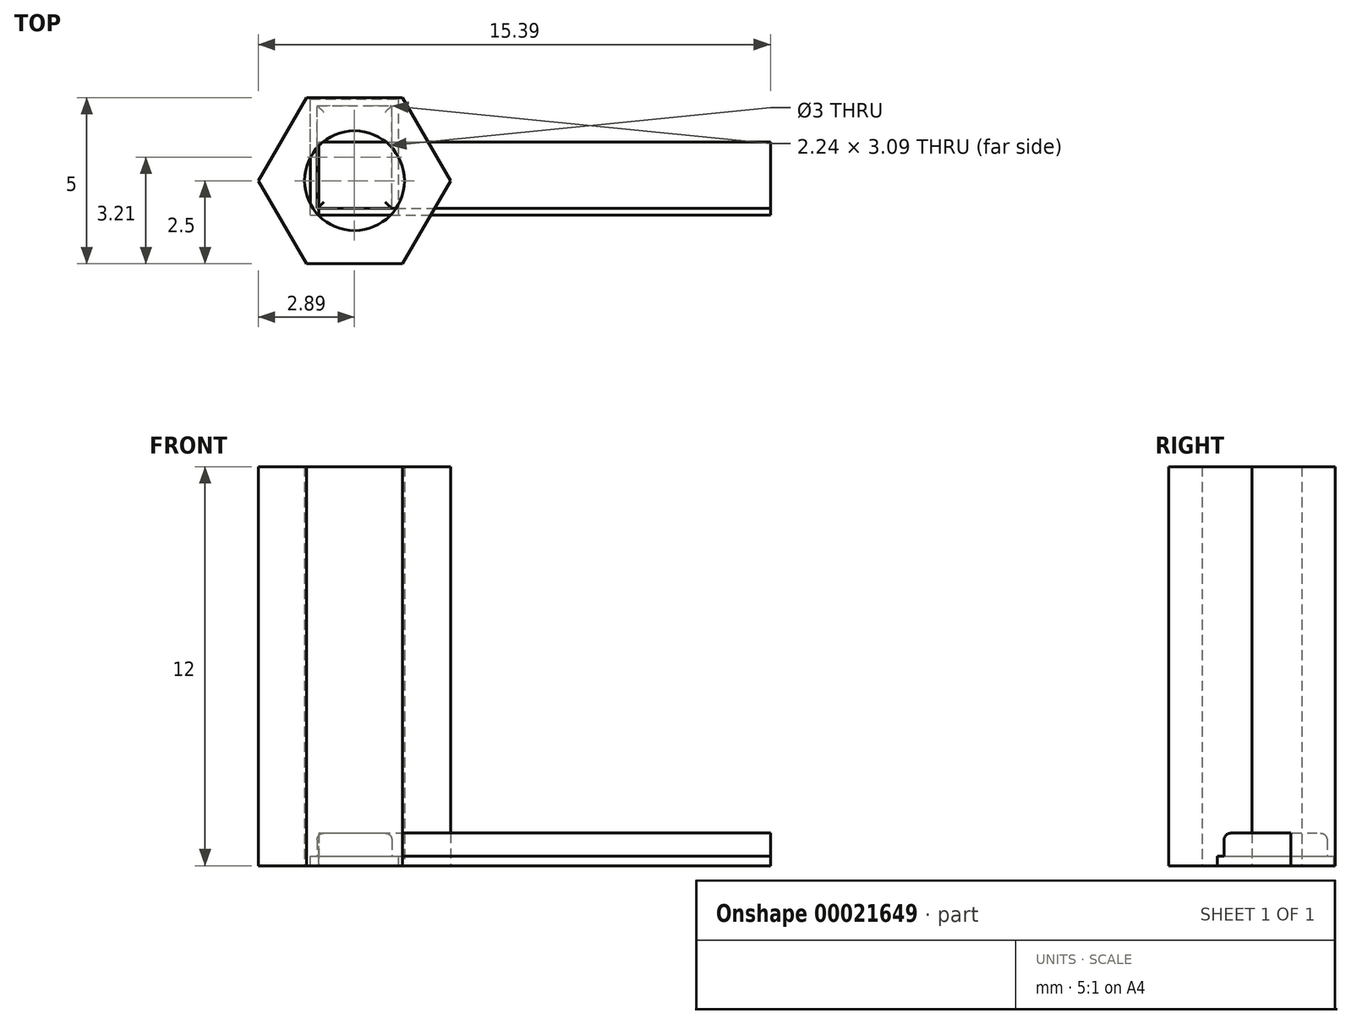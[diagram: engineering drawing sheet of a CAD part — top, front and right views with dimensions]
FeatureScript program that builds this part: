
annotation { "Feature Type Name" : "Feature", "Feature Type Description" : "" }
export const myFeature = defineFeature(function(context is Context, id is Id, definition is map)
    precondition{}
    {
        {
            var Q0;
            Q0=qCreatedBy(makeId("Front.planeOp"),FACE);
            var sketch = newSketch(context, id + "F0", { "sketchPlane" : qUnion([Q0])});
            skLineSegment(sketch, "E0.bottom", {"start": v(-1.12, 0.3) * mm, "end": v(1.12, 0.3) * mm});
            skPoint(sketch, "E1", {"position": v(0, 0.3) * mm});
            skPoint(sketch, "E2.visualSharp", {"position": v(1.12, 0.98) * mm});
            skLineSegment(sketch, "E3.top", {"start": v(-1.32, 0.3) * mm, "end": v(1.32, 0.3) * mm});
            skLineSegment(sketch, "E0.top", {"start": v(-0.92, 0.98) * mm, "end": v(0.92, 0.98) * mm});
            skPoint(sketch, "E4.visualSharp", {"position": v(-1.12, 0.98) * mm});
            skLineSegment(sketch, "E3.bottom", {"start": v(-1.32, 0) * mm, "end": v(1.32, 0) * mm});
            skPoint(sketch, "E5", {"position": v(0, 0) * mm});
            skLineSegment(sketch, "E0.right", {"start": v(1.12, 0.3) * mm, "end": v(1.12, 0.78) * mm});
            skLineSegment(sketch, "E3.left", {"start": v(-1.32, 0) * mm, "end": v(-1.32, 0.3) * mm});
            skLineSegment(sketch, "E0.left", {"start": v(-1.12, 0.3) * mm, "end": v(-1.12, 0.78) * mm});
            skLineSegment(sketch, "E3.right", {"start": v(1.32, 0) * mm, "end": v(1.32, 0.3) * mm});
            skArc(sketch, "E2.filletArc", {"start": v(1.12, 0.78) * mm, "mid": v(1.06, 0.92) * mm, "end": v(0.92, 0.98) * mm});
            skArc(sketch, "E4.filletArc", {"start": v(-0.92, 0.98) * mm, "mid": v(-1.06, 0.92) * mm, "end": v(-1.12, 0.78) * mm});
            skLineSegment(sketch, "E6.bottom", {"start": v(-0.13, 0) * mm, "end": v(0.13, 0) * mm, "construction": true});
            skLineSegment(sketch, "E6.top", {"start": v(-0.12, 0.3) * mm, "end": v(0.12, 0.3) * mm, "construction": true});
            skLineSegment(sketch, "E6.left", {"start": v(-0.13, 0) * mm, "end": v(-0.12, 0.3) * mm, "construction": true});
            skLineSegment(sketch, "E6.right", {"start": v(0.12, 0) * mm, "end": v(0.13, 0.3) * mm, "construction": true});
            skSolve(sketch);
        }
        {
            var Q0;
            Q0=qCreatedBy(makeId("Right.planeOp"),FACE);
            var sketch = newSketch(context, id + "F1", { "sketchPlane" : qUnion([Q0])});
            skLineSegment(sketch, "E7.bottom", {"start": v(-0.84, 0.3) * mm, "end": v(2.26, 0.3) * mm});
            skPoint(sketch, "E8", {"position": v(0, 0.3) * mm});
            skPoint(sketch, "E9.visualSharp", {"position": v(2.26, 0.98) * mm});
            skLineSegment(sketch, "E10.top", {"start": v(-1.04, 0.3) * mm, "end": v(2.46, 0.3) * mm});
            skLineSegment(sketch, "E7.top", {"start": v(-0.64, 0.98) * mm, "end": v(2.06, 0.98) * mm});
            skPoint(sketch, "E11.visualSharp", {"position": v(-0.84, 0.98) * mm});
            skLineSegment(sketch, "E10.bottom", {"start": v(-1.04, 0) * mm, "end": v(2.46, 0) * mm});
            skPoint(sketch, "E12", {"position": v(0, 0) * mm});
            skLineSegment(sketch, "E7.right", {"start": v(2.26, 0.3) * mm, "end": v(2.26, 0.78) * mm});
            skLineSegment(sketch, "E10.left", {"start": v(-1.04, 0) * mm, "end": v(-1.04, 0.3) * mm});
            skLineSegment(sketch, "E7.left", {"start": v(-0.84, 0.3) * mm, "end": v(-0.84, 0.78) * mm});
            skLineSegment(sketch, "E10.right", {"start": v(2.46, 0) * mm, "end": v(2.46, 0.3) * mm});
            skArc(sketch, "E9.filletArc", {"start": v(2.26, 0.78) * mm, "mid": v(2.2, 0.92) * mm, "end": v(2.06, 0.98) * mm});
            skArc(sketch, "E11.filletArc", {"start": v(-0.64, 0.98) * mm, "mid": v(-0.78, 0.92) * mm, "end": v(-0.84, 0.78) * mm});
            skLineSegment(sketch, "E13.bottom", {"start": v(-0.12, 0) * mm, "end": v(0.12, 0) * mm, "construction": true});
            skLineSegment(sketch, "E13.top", {"start": v(-0.12, 0.3) * mm, "end": v(0.13, 0.3) * mm, "construction": true});
            skLineSegment(sketch, "E13.left", {"start": v(-0.12, 0) * mm, "end": v(-0.12, 0.3) * mm, "construction": true});
            skLineSegment(sketch, "E13.right", {"start": v(0.13, 0) * mm, "end": v(0.13, 0.3) * mm, "construction": true});
            skPoint(sketch, "E14", {"position": v(0.71, 0.3) * mm});
            skPoint(sketch, "E15", {"position": v(0.7, 0.98) * mm});
            skSolve(sketch);
        }
        {
            var Q0;
            Q0=qCreatedBy(makeId("Right.planeOp"),FACE);
            var sketch = newSketch(context, id + "F2", { "sketchPlane" : qUnion([Q0])});
            skLineSegment(sketch, "E16", {"start": v(0.32, 7.81) * mm, "end": v(0, 8.13) * mm});
            skLineSegment(sketch, "E17", {"start": v(1.17, 2.29) * mm, "end": v(1.17, 0) * mm});
            skLineSegment(sketch, "E18.MirrorCS", {"start": v(-1.17, 2.29) * mm, "end": v(-1.17, 0) * mm});
            skLineSegment(sketch, "E19", {"start": v(0, 8.13) * mm, "end": v(-0.32, 7.81) * mm});
            skLineSegment(sketch, "E20", {"start": v(-0.32, 7.81) * mm, "end": v(0.32, 7.81) * mm});
            skLineSegment(sketch, "E21", {"start": v(0, -5.48) * mm, "end": v(0, 11.54) * mm, "construction": true});
            skLineSegment(sketch, "E22", {"start": v(-1.17, 0) * mm, "end": v(1.17, 0) * mm});
            skPoint(sketch, "E23", {"position": v(0, 0) * mm});
            skLineSegment(sketch, "E24", {"start": v(-1.17, 2.29) * mm, "end": v(1.17, 2.29) * mm});
            skLineSegment(sketch, "E25", {"start": v(-0.32, 7.81) * mm, "end": v(-0.32, -1.97) * mm});
            skLineSegment(sketch, "E26", {"start": v(-0.32, -1.97) * mm, "end": v(0, -2.29) * mm});
            skLineSegment(sketch, "E27", {"start": v(0.32, 7.81) * mm, "end": v(0.32, -1.97) * mm});
            skLineSegment(sketch, "E28", {"start": v(0.32, -1.97) * mm, "end": v(0, -2.29) * mm});
            skLineSegment(sketch, "E29", {"start": v(0.32, -1.97) * mm, "end": v(-0.32, -1.97) * mm});
            skSolve(sketch);
        }
        {
            var Q0;
            Q0=qCreatedBy(makeId("Top.planeOp"),FACE);
            var sketch = newSketch(context, id + "F3", { "sketchPlane" : qUnion([Q0])});
            skCircle(sketch, "E30.cCircle", {"center": v(0, 0) * mm, "radius": 2.5 * mm, "construction": true});
            skLineSegment(sketch, "E30.0", {"start": v(2.89, 0) * mm, "end": v(1.44, -2.5) * mm});
            skLineSegment(sketch, "E30.1", {"start": v(1.44, -2.5) * mm, "end": v(-1.44, -2.5) * mm});
            skLineSegment(sketch, "E30.2", {"start": v(-1.44, -2.5) * mm, "end": v(-2.89, 0) * mm});
            skLineSegment(sketch, "E30.3", {"start": v(-2.89, 0) * mm, "end": v(-1.44, 2.5) * mm});
            skLineSegment(sketch, "E30.4", {"start": v(-1.44, 2.5) * mm, "end": v(1.44, 2.5) * mm});
            skLineSegment(sketch, "E30.5", {"start": v(1.44, 2.5) * mm, "end": v(2.89, 0) * mm});
            skPoint(sketch, "E30.0.midPoint", {"position": v(2.17, -1.25) * mm});
            skCircle(sketch, "E31", {"center": v(0, 0) * mm, "radius": 1.5 * mm});
            skSolve(sketch);
        }
        {
            var Q0;
            Q0=qCreatedBy(makeId("Front.planeOp"),FACE);
            var sketch = newSketch(context, id + "F4", { "sketchPlane" : qUnion([Q0])});
            skPoint(sketch, "E32.0", {"position": v(0, 8.13) * mm});
            skPoint(sketch, "E33.0", {"position": v(0, -2.29) * mm});
            skLineSegment(sketch, "E34", {"start": v(-1.07, 0) * mm, "end": v(13.77, 0) * mm});
            skLineSegment(sketch, "E35", {"start": v(13.77, 2.29) * mm, "end": v(-1.07, 2.29) * mm});
            skLineSegment(sketch, "E36", {"start": v(-1.07, 2.29) * mm, "end": v(-1.07, 0) * mm});
            skLineSegment(sketch, "E37", {"start": v(13.77, 0) * mm, "end": v(13.77, 2.29) * mm});
            skLineSegment(sketch, "E38", {"start": v(0, -2.29) * mm, "end": v(0.32, -1.97) * mm});
            skLineSegment(sketch, "E39", {"start": v(0.32, -1.97) * mm, "end": v(-0.32, -1.97) * mm});
            skLineSegment(sketch, "E40", {"start": v(-0.32, -1.97) * mm, "end": v(0, -2.29) * mm});
            skLineSegment(sketch, "E41", {"start": v(0, 8.13) * mm, "end": v(-0.32, 7.81) * mm});
            skLineSegment(sketch, "E42", {"start": v(-0.32, 7.81) * mm, "end": v(0.32, 7.81) * mm});
            skLineSegment(sketch, "E43", {"start": v(0.32, 7.81) * mm, "end": v(0, 8.13) * mm});
            skLineSegment(sketch, "E44", {"start": v(-0.32, 7.81) * mm, "end": v(-0.32, -1.97) * mm});
            skLineSegment(sketch, "E45", {"start": v(0.32, -1.97) * mm, "end": v(0.32, 7.81) * mm});
            skPoint(sketch, "E46.0", {"position": v(0, 7.81) * mm});
            skPoint(sketch, "E47.0", {"position": v(0, 2.29) * mm});
            skSolve(sketch);
        }
        {
            var Q0;
            {var subQ5=sQuery(id+"F4.wireOp",EDGE,"E37");Q0=makeQuery(id+"F4.imprint","IMPRINT",FACE,{"disambiguationData":[TD([[makeQuery(id+"F4.imprint","IMPRINT",EDGE,{"derivedFrom":subQ5}),1.0]])]});}
            var Q1;
            {var subQ5=sQuery(id+"F4.wireOp",EDGE,"E36");Q1=makeQuery(id+"F4.imprint","IMPRINT",FACE,{"disambiguationData":[TD([[makeQuery(id+"F4.imprint","IMPRINT",EDGE,{"derivedFrom":subQ5}),1.0]])]});}
            var Q2;
            {var subQ3=sQuery(id+"F4.wireOp",EDGE,"E34");var subQ5=sQuery(id+"F4.wireOp",EDGE,"E44");var subQ7=makeQuery(id+"F4.imprint","INTERSECT",VERTEX,{"derivedFrom":[subQ3,subQ5]});Q2=makeQuery(id+"F4.imprint","IMPRINT",FACE,{"disambiguationData":[TD([[makeQuery(id+"F4.imprint","IMPRINT",EDGE,{"disambiguationData":[TD([[subQ7,-1.0]])],"derivedFrom":subQ3}),1.0]])]});}
            extrude(context, id + "F5", {"entities" : qUnion([Q0, Q1, Q2]), "endBound" : BoundingType.SYMMETRIC, "depth" : 2.34 * mm});
        }
        {
            var Q0;
            Q0=makeQuery(id+"F0.imprint","IMPRINT",FACE,{"disambiguationData":[TD([[makeQuery(id+"F0.imprint","IMPRINT",EDGE,{"derivedFrom":sQuery(id+"F0.wireOp",EDGE,"E3.bottom")}),1.0]])]});
            var Q1;
            Q1=makeQuery(id+"F0.imprint","IMPRINT",FACE,{"disambiguationData":[TD([[makeQuery(id+"F0.imprint","IMPRINT",EDGE,{"derivedFrom":sQuery(id+"F0.wireOp",EDGE,"E0.top")}),-1.0]])]});
            extrude(context, id + "F6", {"entities" : qUnion([Q0, Q1]), "depth" : 1.04 * mm, "hasSecondDirection" : true, "secondDirectionOppositeDirection" : true, "secondDirectionDepth" : 2.46 * mm});
        }
        {
            var Q0;
            Q0=makeQuery(id+"F1.imprint","IMPRINT",FACE,{"disambiguationData":[TD([[makeQuery(id+"F1.imprint","IMPRINT",EDGE,{"derivedFrom":sQuery(id+"F1.wireOp",EDGE,"E7.top")}),-1.0]])]});
            var Q1;
            Q1=makeQuery(id+"F1.imprint","IMPRINT",FACE,{"disambiguationData":[TD([[makeQuery(id+"F1.imprint","IMPRINT",EDGE,{"derivedFrom":sQuery(id+"F1.wireOp",EDGE,"E10.bottom")}),1.0]])]});
            extrude(context, id + "F7", {"entities" : qUnion([Q0, Q1]), "operationType" : NewBodyOperationType.INTERSECT, "endBound" : BoundingType.SYMMETRIC, "oppositeDirection" : true, "depth" : 25 * mm});
        }
        {
            var Q0;
            Q0=makeQuery(id+"F3.imprint","IMPRINT",FACE,{"disambiguationData":[TD([[makeQuery(id+"F3.imprint","IMPRINT",EDGE,{"derivedFrom":sQuery(id+"F3.wireOp",EDGE,"E30.0")}),-1.0]])]});
            extrude(context, id + "F8", {"entities" : qUnion([Q0]), "depth" : 12 * mm});
        }
        {
            var Q0;
            Q0=makeQuery(id+"F6.opExtrude","SWEPT_BODY",BODY,{"disambiguationData":[OSD([sQuery(id+"F0.wireOp",EDGE,"E3.top"),sQuery(id+"F0.wireOp",EDGE,"E0.top"),sQuery(id+"F0.wireOp",EDGE,"E3.bottom"),sQuery(id+"F0.wireOp",EDGE,"E0.right"),sQuery(id+"F0.wireOp",EDGE,"E3.left"),sQuery(id+"F0.wireOp",EDGE,"E0.left"),sQuery(id+"F0.wireOp",EDGE,"E3.right"),sQuery(id+"F0.wireOp",EDGE,"E2.filletArc"),sQuery(id+"F0.wireOp",EDGE,"E4.filletArc")])]});
            transform(context, id + "F9", {"entities" : qUnion([Q0]), "transformType" : TransformType.TRANSLATION_3D, "dx" : 0 * mm, "dy" : 0 * mm, "dz" : 0 * mm, "makeCopy" : true});
        }
    });
